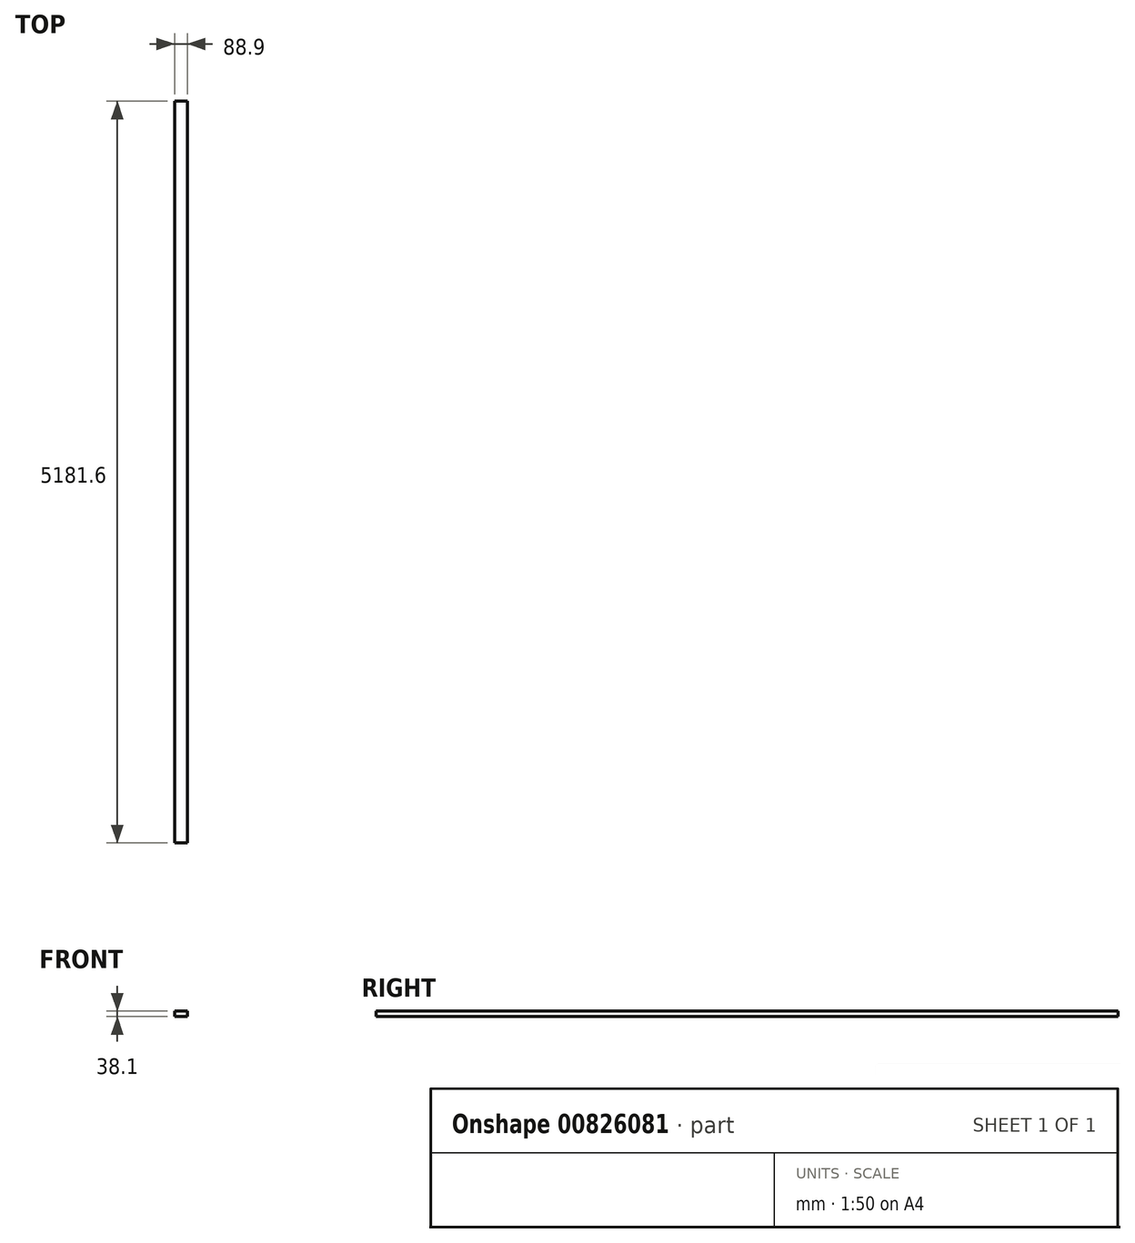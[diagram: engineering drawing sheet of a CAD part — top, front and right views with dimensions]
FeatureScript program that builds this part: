
annotation { "Feature Type Name" : "Feature", "Feature Type Description" : "" }
export const myFeature = defineFeature(function(context is Context, id is Id, definition is map)
    precondition{}
    {
        {
            var Q0;
            Q0=qCreatedBy(makeId("Top.planeOp"),FACE);
            var sketch = newSketch(context, id + "F0", { "sketchPlane" : qUnion([Q0])});
            skLineSegment(sketch, "E0.bottom", {"start": v(-29.27, 0) * mm, "end": v(59.63, 0) * mm});
            skLineSegment(sketch, "E0.top", {"start": v(-29.27, 5181.6) * mm, "end": v(59.63, 5181.6) * mm});
            skLineSegment(sketch, "E0.left", {"start": v(-29.27, 0) * mm, "end": v(-29.27, 5181.6) * mm});
            skLineSegment(sketch, "E0.right", {"start": v(59.63, 0) * mm, "end": v(59.63, 5181.6) * mm});
            skSolve(sketch);
        }
        {
            var Q0;
            Q0=qSketchRegion(id+"F0",true);
            extrude(context, id + "F1", {"entities" : qUnion([Q0]), "depth" : 38.1 * mm, "offsetDistance" : 25.4 * mm});
        }
    });
